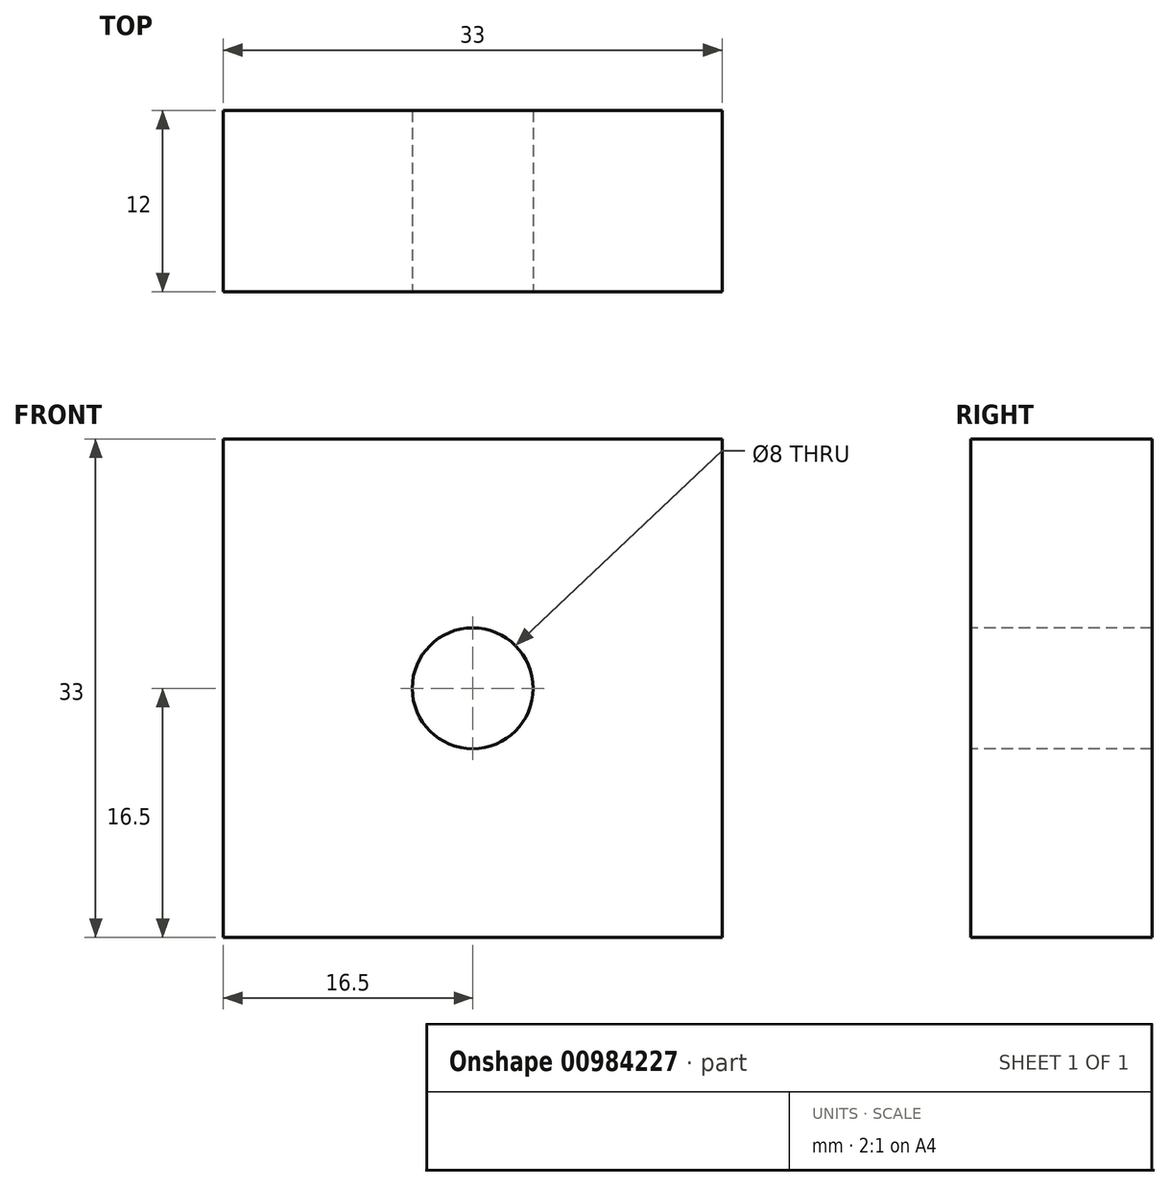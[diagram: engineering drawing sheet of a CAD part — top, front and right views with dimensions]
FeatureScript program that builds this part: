
annotation { "Feature Type Name" : "Feature", "Feature Type Description" : "" }
export const myFeature = defineFeature(function(context is Context, id is Id, definition is map)
    precondition{}
    {
        {
            var Q0;
            Q0=qCreatedBy(makeId("Front.planeOp"),FACE);
            var sketch = newSketch(context, id + "F0", { "sketchPlane" : qUnion([Q0])});
            skLineSegment(sketch, "E0.bottom", {"start": v(16.5, 16.5) * mm, "end": v(-16.5, 16.5) * mm});
            skLineSegment(sketch, "E0.top", {"start": v(16.5, -16.5) * mm, "end": v(-16.5, -16.5) * mm});
            skLineSegment(sketch, "E0.left", {"start": v(16.5, 16.5) * mm, "end": v(16.5, -16.5) * mm});
            skLineSegment(sketch, "E0.right", {"start": v(-16.5, 16.5) * mm, "end": v(-16.5, -16.5) * mm});
            skPoint(sketch, "E0.middle", {"position": v(0, 0) * mm});
            skSolve(sketch);
        }
        {
            var Q0;
            Q0=makeQuery(id+"F0.imprint","IMPRINT",FACE,{"disambiguationData":[TD([[makeQuery(id+"F0.imprint","IMPRINT",EDGE,{"derivedFrom":sQuery(id+"F0.wireOp",EDGE,"E0.bottom")}),1.0]])]});
            extrude(context, id + "F1", {"entities" : qUnion([Q0]), "oppositeDirection" : true, "depth" : 12 * mm, "offsetDistance" : 25 * mm});
        }
        {
            var Q0;
            Q0=makeQuery(id+"F1.opExtrude","CAP_FACE",FACE,{"disambiguationData":[OSD([sQuery(id+"F0.wireOp",EDGE,"E0.bottom"),sQuery(id+"F0.wireOp",EDGE,"E0.top"),sQuery(id+"F0.wireOp",EDGE,"E0.left"),sQuery(id+"F0.wireOp",EDGE,"E0.right")])],"isStart":true});
            var sketch = newSketch(context, id + "F2", { "sketchPlane" : qUnion([Q0])});
            skCircle(sketch, "E1", {"center": v(0, 0) * mm, "radius": 4 * mm});
            skSolve(sketch);
        }
        {
            var Q0;
            Q0=makeQuery(id+"F2.imprint","IMPRINT",FACE,{"disambiguationData":[TD([[makeQuery(id+"F2.imprint","IMPRINT",EDGE,{"derivedFrom":sQuery(id+"F2.wireOp",EDGE,"E1")}),1.0]])]});
            extrude(context, id + "F3", {"entities" : qUnion([Q0]), "operationType" : NewBodyOperationType.REMOVE, "oppositeDirection" : true, "depth" : 12 * mm, "offsetDistance" : 25 * mm});
        }
    });
